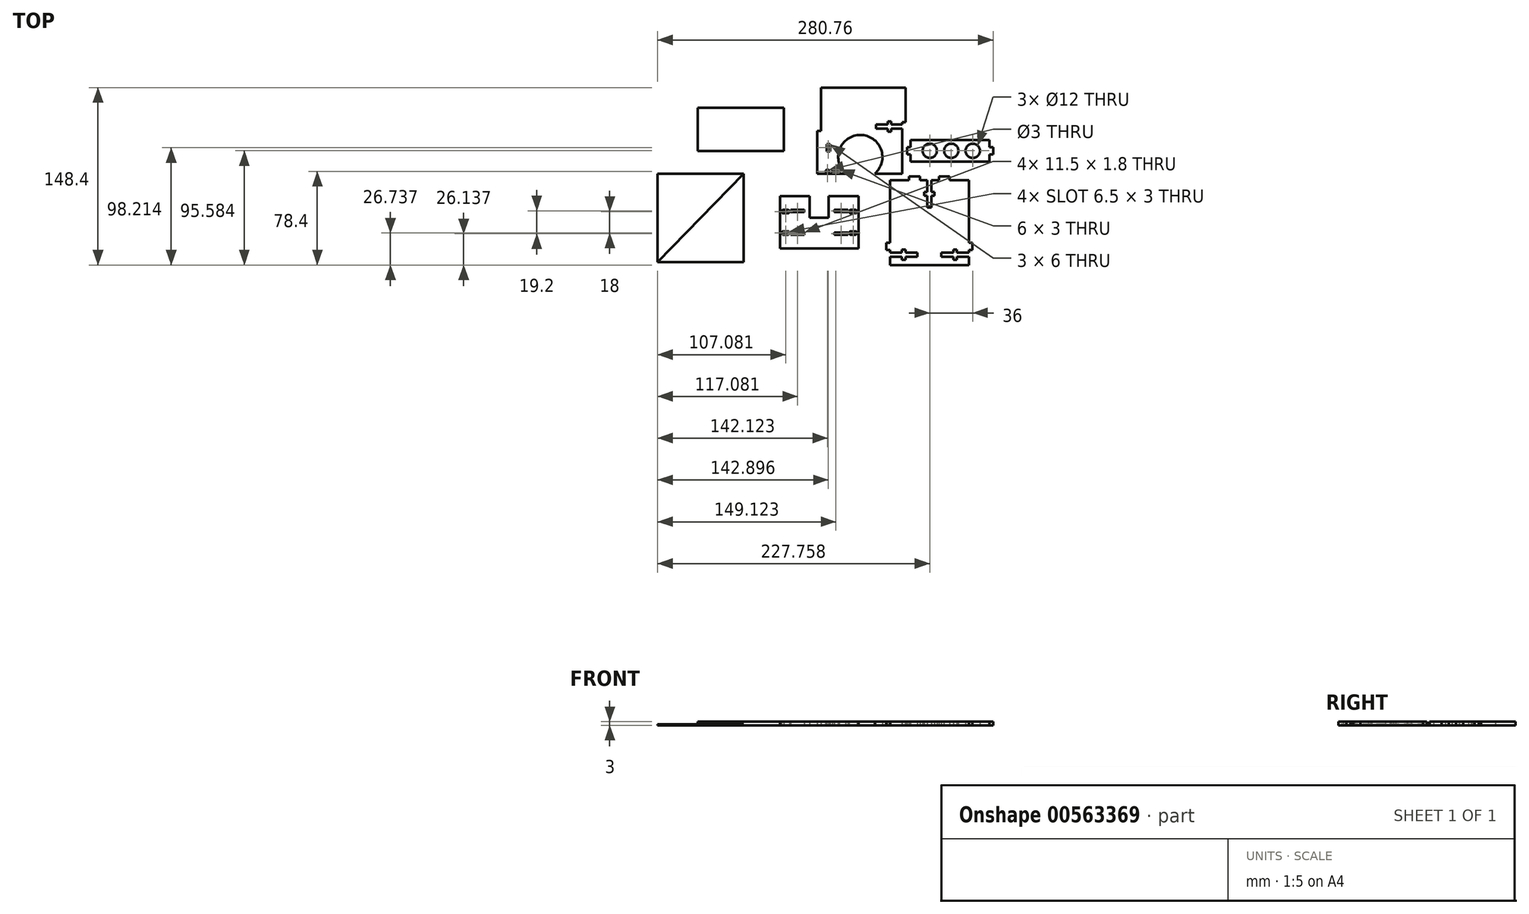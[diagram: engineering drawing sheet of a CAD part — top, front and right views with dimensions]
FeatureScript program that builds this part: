
annotation { "Feature Type Name" : "Feature", "Feature Type Description" : "" }
export const myFeature = defineFeature(function(context is Context, id is Id, definition is map)
    precondition{}
    {
        {
            var Q0;
            Q0=qCreatedBy(makeId("Top.planeOp"),FACE);
            var sketch = newSketch(context, id + "F0", { "sketchPlane" : qUnion([Q0])});
            skLineSegment(sketch, "E0", {"start": v(0, 0) * mm, "end": v(31.91, 0) * mm});
            skLineSegment(sketch, "E1", {"start": v(31.91, 0) * mm, "end": v(31.91, 36) * mm});
            skLineSegment(sketch, "E2", {"start": v(31.91, 36) * mm, "end": v(34.91, 36) * mm});
            skLineSegment(sketch, "E3", {"start": v(34.91, 36) * mm, "end": v(34.91, 72) * mm});
            skLineSegment(sketch, "E4", {"start": v(34.91, 72) * mm, "end": v(-36.09, 72) * mm});
            skLineSegment(sketch, "E5", {"start": v(-36.09, 72) * mm, "end": v(-36.09, 36) * mm});
            skLineSegment(sketch, "E6", {"start": v(-36.09, 36) * mm, "end": v(-39.09, 36) * mm});
            skLineSegment(sketch, "E7", {"start": v(-39.09, 36) * mm, "end": v(-39.09, 0) * mm});
            skLineSegment(sketch, "E8", {"start": v(-39.09, 0) * mm, "end": v(0, 0) * mm});
            skSolve(sketch);
        }
        {
            var Q0;
            Q0=makeQuery(id+"F0.imprint","IMPRINT",FACE,{"disambiguationData":[TD([[makeQuery(id+"F0.imprint","IMPRINT",EDGE,{"derivedFrom":sQuery(id+"F0.wireOp",EDGE,"E0")}),1.0]])]});
            extrude(context, id + "F1", {"entities" : qUnion([Q0]), "depth" : 3 * mm});
        }
        {
            var Q0;
            Q0=makeQuery(id+"F0.imprint","IMPRINT",FACE,{"disambiguationData":[TD([[makeQuery(id+"F0.imprint","IMPRINT",EDGE,{"derivedFrom":sQuery(id+"F0.wireOp",EDGE,"E0")}),1.0]])]});
            var sketch = newSketch(context, id + "F2", { "sketchPlane" : qUnion([Q0])});
            skCircle(sketch, "E9", {"center": v(-3.09, 14) * mm, "radius": 18.5 * mm});
            skCircle(sketch, "E10", {"center": v(-30.59, 2) * mm, "radius": 1.5 * mm});
            skLineSegment(sketch, "E11.bottom", {"start": v(-26.59, 3.5) * mm, "end": v(-20.59, 3.5) * mm});
            skLineSegment(sketch, "E11.top", {"start": v(-26.59, 0.5) * mm, "end": v(-20.59, 0.5) * mm});
            skLineSegment(sketch, "E11.left", {"start": v(-26.59, 3.5) * mm, "end": v(-26.59, 0.5) * mm});
            skLineSegment(sketch, "E11.right", {"start": v(-20.59, 3.5) * mm, "end": v(-20.59, 0.5) * mm});
            skLineSegment(sketch, "E12.bottom", {"start": v(-31.31, 24.81) * mm, "end": v(-28.31, 24.81) * mm});
            skLineSegment(sketch, "E12.top", {"start": v(-31.31, 18.81) * mm, "end": v(-28.31, 18.81) * mm});
            skLineSegment(sketch, "E12.left", {"start": v(-31.31, 24.81) * mm, "end": v(-31.31, 18.81) * mm});
            skLineSegment(sketch, "E12.right", {"start": v(-28.31, 24.81) * mm, "end": v(-28.31, 18.81) * mm});
            skSolve(sketch);
        }
        {
            var Q0;
            Q0=qSketchRegion(id+"F2",true);
            extrude(context, id + "F3", {"entities" : qUnion([Q0]), "operationType" : NewBodyOperationType.REMOVE, "endBound" : BoundingType.UP_TO_NEXT, "depth" : 25 * mm});
        }
        {
            var Q0;
            Q0=makeQuery(id+"F1.opExtrude","CAP_FACE",FACE,{"disambiguationData":[OSD([sQuery(id+"F0.wireOp",EDGE,"E0"),sQuery(id+"F0.wireOp",EDGE,"E1"),sQuery(id+"F0.wireOp",EDGE,"E2"),sQuery(id+"F0.wireOp",EDGE,"E3"),sQuery(id+"F0.wireOp",EDGE,"E4"),sQuery(id+"F0.wireOp",EDGE,"E5"),sQuery(id+"F0.wireOp",EDGE,"E6"),sQuery(id+"F0.wireOp",EDGE,"E7"),sQuery(id+"F0.wireOp",EDGE,"E8")])],"isStart":false});
            var sketch = newSketch(context, id + "F4", { "sketchPlane" : qUnion([Q0])});
            skLineSegment(sketch, "E13", {"start": v(22.91, 41.25) * mm, "end": v(22.91, 43.75) * mm});
            skLineSegment(sketch, "E14", {"start": v(22.91, 43.75) * mm, "end": v(19.91, 43.75) * mm});
            skLineSegment(sketch, "E15", {"start": v(19.91, 43.75) * mm, "end": v(19.91, 41.25) * mm});
            skLineSegment(sketch, "E16", {"start": v(19.91, 41.25) * mm, "end": v(9.91, 41.25) * mm});
            skLineSegment(sketch, "E17", {"start": v(9.91, 41.25) * mm, "end": v(9.91, 37.75) * mm});
            skLineSegment(sketch, "E18", {"start": v(9.91, 37.75) * mm, "end": v(19.91, 37.75) * mm});
            skLineSegment(sketch, "E19", {"start": v(19.91, 37.75) * mm, "end": v(19.91, 35.25) * mm});
            skLineSegment(sketch, "E20", {"start": v(19.91, 35.25) * mm, "end": v(22.91, 35.25) * mm});
            skLineSegment(sketch, "E21", {"start": v(22.91, 35.25) * mm, "end": v(22.91, 37.75) * mm});
            skLineSegment(sketch, "E22", {"start": v(22.91, 41.25) * mm, "end": v(31.91, 41.25) * mm});
            skLineSegment(sketch, "E23", {"start": v(31.91, 36) * mm, "end": v(31.91, 37.75) * mm});
            skLineSegment(sketch, "E24", {"start": v(31.91, 37.75) * mm, "end": v(22.91, 37.75) * mm});
            skLineSegment(sketch, "E25", {"start": v(31.91, 41.25) * mm, "end": v(31.91, 43) * mm});
            skLineSegment(sketch, "E26", {"start": v(31.91, 43) * mm, "end": v(34.91, 43) * mm});
            skLineSegment(sketch, "E27", {"start": v(31.91, 36) * mm, "end": v(34.91, 36) * mm});
            skLineSegment(sketch, "E28", {"start": v(34.91, 36) * mm, "end": v(34.91, 43) * mm});
            skSolve(sketch);
        }
        {
            var Q0;
            Q0=makeQuery(id+"F4.imprint","IMPRINT",FACE,{"disambiguationData":[TD([[makeQuery(id+"F4.imprint","IMPRINT",EDGE,{"derivedFrom":sQuery(id+"F4.wireOp",EDGE,"E13")}),1.0]])]});
            var Q1;
            Q1=makeQuery(id+"F4.imprint","IMPRINT",FACE,{"disambiguationData":[TD([[makeQuery(id+"F4.imprint","IMPRINT",EDGE,{"derivedFrom":sQuery(id+"F4.wireOp",EDGE,"a1bc5330-3307-4b1e-8fa0-ecfa6d1ff466.1.0.0")}),1.0]])]});
            extrude(context, id + "F5", {"entities" : qUnion([Q0, Q1]), "operationType" : NewBodyOperationType.REMOVE, "endBound" : BoundingType.UP_TO_NEXT, "oppositeDirection" : true, "depth" : 25 * mm});
        }
        {
            var Q0;
            Q0=qCreatedBy(makeId("Top.planeOp"),FACE);
            var sketch = newSketch(context, id + "F6", { "sketchPlane" : qUnion([Q0])});
            skLineSegment(sketch, "E29.bottom", {"start": v(-70.38, -18.66) * mm, "end": v(-4.38, -18.66) * mm});
            skLineSegment(sketch, "E29.top", {"start": v(-70.38, -62.66) * mm, "end": v(-4.38, -62.66) * mm});
            skLineSegment(sketch, "E29.left", {"start": v(-70.38, -18.66) * mm, "end": v(-70.38, -62.66) * mm});
            skLineSegment(sketch, "E29.right", {"start": v(-4.38, -18.66) * mm, "end": v(-4.38, -62.66) * mm});
            skLineSegment(sketch, "E30.bottom", {"start": v(-61.38, -30.16) * mm, "end": v(-49.88, -30.16) * mm});
            skLineSegment(sketch, "E30.top", {"start": v(-61.38, -31.96) * mm, "end": v(-49.88, -31.96) * mm});
            skLineSegment(sketch, "E30.left", {"start": v(-61.38, -30.16) * mm, "end": v(-61.38, -31.96) * mm});
            skLineSegment(sketch, "E30.right", {"start": v(-49.88, -30.16) * mm, "end": v(-49.88, -31.96) * mm});
            skLineSegment(sketch, "E31.bottom", {"start": v(-67.38, -30.16) * mm, "end": v(-63.88, -30.16) * mm});
            skLineSegment(sketch, "E31.top", {"start": v(-67.38, -33.16) * mm, "end": v(-63.88, -33.16) * mm});
            skLineSegment(sketch, "E31.left", {"start": v(-68.88, -31.66) * mm, "end": v(-68.88, -31.66) * mm});
            skLineSegment(sketch, "E31.right", {"start": v(-62.38, -31.66) * mm, "end": v(-62.38, -31.66) * mm});
            skPoint(sketch, "E32.visualSharp", {"position": v(-68.88, -30.16) * mm});
            skArc(sketch, "E32.filletArc", {"start": v(-67.38, -30.16) * mm, "mid": v(-68.44, -30.6) * mm, "end": v(-68.88, -31.66) * mm});
            skPoint(sketch, "E33.visualSharp", {"position": v(-68.88, -33.16) * mm});
            skArc(sketch, "E33.filletArc", {"start": v(-68.88, -31.66) * mm, "mid": v(-68.44, -32.72) * mm, "end": v(-67.38, -33.16) * mm});
            skPoint(sketch, "E34.visualSharp", {"position": v(-62.38, -33.16) * mm});
            skArc(sketch, "E34.filletArc", {"start": v(-63.88, -33.16) * mm, "mid": v(-62.82, -32.72) * mm, "end": v(-62.38, -31.66) * mm});
            skPoint(sketch, "E35.visualSharp", {"position": v(-62.38, -30.16) * mm});
            skArc(sketch, "E35.filletArc", {"start": v(-62.38, -31.66) * mm, "mid": v(-62.82, -30.6) * mm, "end": v(-63.88, -30.16) * mm});
            skLineSegment(sketch, "E36", {"start": v(-70.38, -40.66) * mm, "end": v(-4.38, -40.66) * mm, "construction": true});
            skLineSegment(sketch, "E37", {"start": v(-37.38, -18.66) * mm, "end": v(-37.38, -62.66) * mm, "construction": true});
            skArc(sketch, "E38.MirrorCS", {"start": v(-12.38, -31.66) * mm, "mid": v(-11.94, -30.6) * mm, "end": v(-10.88, -30.16) * mm});
            skLineSegment(sketch, "E39.MirrorCS", {"start": v(-24.88, -30.16) * mm, "end": v(-24.88, -31.96) * mm});
            skLineSegment(sketch, "E40.MirrorCS", {"start": v(-13.38, -30.16) * mm, "end": v(-13.38, -31.96) * mm});
            skArc(sketch, "E41.MirrorCS", {"start": v(-10.88, -33.16) * mm, "mid": v(-11.94, -32.72) * mm, "end": v(-12.38, -31.66) * mm});
            skArc(sketch, "E42.MirrorCS", {"start": v(-5.88, -31.66) * mm, "mid": v(-6.32, -32.72) * mm, "end": v(-7.38, -33.16) * mm});
            skArc(sketch, "E43.MirrorCS", {"start": v(-7.38, -30.16) * mm, "mid": v(-6.32, -30.6) * mm, "end": v(-5.88, -31.66) * mm});
            skLineSegment(sketch, "E44.MirrorCS", {"start": v(-7.38, -30.16) * mm, "end": v(-10.88, -30.16) * mm});
            skLineSegment(sketch, "E45.MirrorCS", {"start": v(-7.38, -33.16) * mm, "end": v(-10.88, -33.16) * mm});
            skLineSegment(sketch, "E46.MirrorCS", {"start": v(-13.38, -30.16) * mm, "end": v(-24.88, -30.16) * mm});
            skLineSegment(sketch, "E47.MirrorCS", {"start": v(-13.38, -31.96) * mm, "end": v(-24.88, -31.96) * mm});
            skPoint(sketch, "E48.MirrorP", {"position": v(-12.38, -33.16) * mm});
            skPoint(sketch, "E49.MirrorP", {"position": v(-12.38, -30.16) * mm});
            skPoint(sketch, "E50.MirrorP", {"position": v(-5.88, -30.16) * mm});
            skPoint(sketch, "E51.MirrorP", {"position": v(-5.88, -33.16) * mm});
            skLineSegment(sketch, "E52.MirrorCS", {"start": v(-7.38, -51.16) * mm, "end": v(-10.88, -51.16) * mm});
            skLineSegment(sketch, "E53.MirrorCS", {"start": v(-7.38, -48.16) * mm, "end": v(-10.88, -48.16) * mm});
            skLineSegment(sketch, "E54.MirrorCS", {"start": v(-13.38, -51.16) * mm, "end": v(-24.88, -51.16) * mm});
            skLineSegment(sketch, "E55.MirrorCS", {"start": v(-13.38, -49.36) * mm, "end": v(-24.88, -49.36) * mm});
            skArc(sketch, "E56.MirrorCS", {"start": v(-62.38, -49.66) * mm, "mid": v(-62.82, -50.72) * mm, "end": v(-63.88, -51.16) * mm});
            skArc(sketch, "E57.MirrorCS", {"start": v(-63.88, -48.16) * mm, "mid": v(-62.82, -48.6) * mm, "end": v(-62.38, -49.66) * mm});
            skArc(sketch, "E58.MirrorCS", {"start": v(-68.88, -49.66) * mm, "mid": v(-68.44, -48.6) * mm, "end": v(-67.38, -48.16) * mm});
            skLineSegment(sketch, "E59.MirrorCS", {"start": v(-61.38, -51.16) * mm, "end": v(-61.38, -49.36) * mm});
            skLineSegment(sketch, "E60.MirrorCS", {"start": v(-49.88, -51.16) * mm, "end": v(-49.88, -49.36) * mm});
            skArc(sketch, "E61.MirrorCS", {"start": v(-67.38, -51.16) * mm, "mid": v(-68.44, -50.72) * mm, "end": v(-68.88, -49.66) * mm});
            skPoint(sketch, "E62.MirrorP", {"position": v(-62.38, -48.16) * mm});
            skPoint(sketch, "E63.MirrorP", {"position": v(-68.88, -48.16) * mm});
            skPoint(sketch, "E64.MirrorP", {"position": v(-62.38, -51.16) * mm});
            skLineSegment(sketch, "E65.MirrorCS", {"start": v(-67.38, -51.16) * mm, "end": v(-63.88, -51.16) * mm});
            skPoint(sketch, "E66.MirrorP", {"position": v(-68.88, -51.16) * mm});
            skLineSegment(sketch, "E67.MirrorCS", {"start": v(-67.38, -48.16) * mm, "end": v(-63.88, -48.16) * mm});
            skLineSegment(sketch, "E68.MirrorCS", {"start": v(-61.38, -49.36) * mm, "end": v(-49.88, -49.36) * mm});
            skLineSegment(sketch, "E69.MirrorCS", {"start": v(-61.38, -51.16) * mm, "end": v(-49.88, -51.16) * mm});
            skArc(sketch, "E70.MirrorCS", {"start": v(-7.38, -51.16) * mm, "mid": v(-6.32, -50.72) * mm, "end": v(-5.88, -49.66) * mm});
            skLineSegment(sketch, "E71.MirrorCS", {"start": v(-13.38, -51.16) * mm, "end": v(-13.38, -49.36) * mm});
            skLineSegment(sketch, "E72.MirrorCS", {"start": v(-24.88, -51.16) * mm, "end": v(-24.88, -49.36) * mm});
            skArc(sketch, "E73.MirrorCS", {"start": v(-10.88, -48.16) * mm, "mid": v(-11.94, -48.6) * mm, "end": v(-12.38, -49.66) * mm});
            skArc(sketch, "E74.MirrorCS", {"start": v(-12.38, -49.66) * mm, "mid": v(-11.94, -50.72) * mm, "end": v(-10.88, -51.16) * mm});
            skArc(sketch, "E75.MirrorCS", {"start": v(-5.88, -49.66) * mm, "mid": v(-6.32, -48.6) * mm, "end": v(-7.38, -48.16) * mm});
            skLineSegment(sketch, "E76.bottom", {"start": v(-45.43, -18.66) * mm, "end": v(-29.7, -18.66) * mm});
            skLineSegment(sketch, "E76.top", {"start": v(-45.43, -36.8) * mm, "end": v(-29.7, -36.8) * mm});
            skLineSegment(sketch, "E76.left", {"start": v(-45.43, -18.66) * mm, "end": v(-45.43, -36.8) * mm});
            skLineSegment(sketch, "E76.right", {"start": v(-29.7, -18.66) * mm, "end": v(-29.7, -36.8) * mm});
            skSolve(sketch);
        }
        {
            var Q0;
            Q0=makeQuery(id+"F6.imprint","IMPRINT",FACE,{"disambiguationData":[TD([[makeQuery(id+"F6.imprint","IMPRINT",EDGE,{"derivedFrom":sQuery(id+"F6.wireOp",EDGE,"E29.bottom")}),-1.0]])]});
            extrude(context, id + "F7", {"entities" : qUnion([Q0]), "depth" : 3 * mm});
        }
        {
            var Q0;
            Q0=qCreatedBy(makeId("Top.planeOp"),FACE);
            var sketch = newSketch(context, id + "F8", { "sketchPlane" : qUnion([Q0])});
            skLineSegment(sketch, "E77.bottom", {"start": v(-67.1, 19.07) * mm, "end": v(-139.1, 19.07) * mm});
            skLineSegment(sketch, "E77.top", {"start": v(-67.1, 55.07) * mm, "end": v(-139.1, 55.07) * mm});
            skLineSegment(sketch, "E77.left", {"start": v(-67.1, 19.07) * mm, "end": v(-67.1, 55.07) * mm});
            skLineSegment(sketch, "E77.right", {"start": v(-139.1, 19.07) * mm, "end": v(-139.1, 55.07) * mm});
            skSolve(sketch);
        }
        {
            var Q0;
            Q0=makeQuery(id+"F8.imprint","IMPRINT",FACE,{"disambiguationData":[TD([[makeQuery(id+"F8.imprint","IMPRINT",EDGE,{"derivedFrom":sQuery(id+"F8.wireOp",EDGE,"E77.bottom")}),-1.0]])]});
            extrude(context, id + "F9", {"entities" : qUnion([Q0]), "depth" : 3 * mm});
        }
        {
            var Q0;
            Q0=qCreatedBy(makeId("Top.planeOp"),FACE);
            var sketch = newSketch(context, id + "F10", { "sketchPlane" : qUnion([Q0])});
            skLineSegment(sketch, "E78.bottom", {"start": v(21.76, -5.4) * mm, "end": v(37.76, -5.4) * mm});
            skLineSegment(sketch, "E78.top", {"start": v(21.76, -76.4) * mm, "end": v(87.76, -76.4) * mm});
            skLineSegment(sketch, "E78.left", {"start": v(21.76, -5.4) * mm, "end": v(21.76, -57.9) * mm});
            skLineSegment(sketch, "E78.right", {"start": v(87.76, -5.4) * mm, "end": v(87.76, -57.9) * mm});
            skLineSegment(sketch, "E79", {"start": v(53.01, -5.4) * mm, "end": v(53.01, -15.4) * mm});
            skLineSegment(sketch, "E80", {"start": v(53.01, -15.4) * mm, "end": v(50.51, -15.4) * mm});
            skLineSegment(sketch, "E81", {"start": v(50.51, -15.4) * mm, "end": v(50.51, -18.4) * mm});
            skLineSegment(sketch, "E82", {"start": v(50.51, -18.4) * mm, "end": v(53.01, -18.4) * mm});
            skLineSegment(sketch, "E83", {"start": v(53.01, -18.4) * mm, "end": v(53.01, -28.4) * mm});
            skLineSegment(sketch, "E84", {"start": v(53.01, -28.4) * mm, "end": v(56.51, -28.4) * mm});
            skLineSegment(sketch, "E85", {"start": v(56.51, -28.4) * mm, "end": v(56.51, -18.4) * mm});
            skLineSegment(sketch, "E86", {"start": v(56.51, -18.4) * mm, "end": v(59.01, -18.4) * mm});
            skLineSegment(sketch, "E87", {"start": v(59.01, -18.4) * mm, "end": v(59.01, -15.4) * mm});
            skLineSegment(sketch, "E88", {"start": v(59.01, -15.4) * mm, "end": v(56.51, -15.4) * mm});
            skLineSegment(sketch, "E89", {"start": v(56.51, -15.4) * mm, "end": v(56.51, -5.4) * mm});
            skLineSegment(sketch, "E90", {"start": v(50.51, -15.4) * mm, "end": v(21.76, -15.4) * mm, "construction": true});
            skLineSegment(sketch, "E91", {"start": v(59.01, -15.4) * mm, "end": v(87.76, -15.4) * mm, "construction": true});
            skLineSegment(sketch, "E92", {"start": v(21.76, -69.65) * mm, "end": v(31.76, -69.65) * mm});
            skLineSegment(sketch, "E93", {"start": v(31.76, -69.65) * mm, "end": v(31.76, -72.15) * mm});
            skLineSegment(sketch, "E94", {"start": v(31.76, -72.15) * mm, "end": v(34.76, -72.15) * mm});
            skLineSegment(sketch, "E95", {"start": v(34.76, -72.15) * mm, "end": v(34.76, -69.65) * mm});
            skLineSegment(sketch, "E96", {"start": v(34.76, -69.65) * mm, "end": v(44.76, -69.65) * mm});
            skLineSegment(sketch, "E97", {"start": v(44.76, -69.65) * mm, "end": v(44.76, -66.15) * mm});
            skLineSegment(sketch, "E98", {"start": v(44.76, -66.15) * mm, "end": v(34.76, -66.15) * mm});
            skLineSegment(sketch, "E99", {"start": v(34.76, -66.15) * mm, "end": v(34.76, -63.65) * mm});
            skLineSegment(sketch, "E100", {"start": v(34.76, -63.65) * mm, "end": v(31.76, -63.65) * mm});
            skLineSegment(sketch, "E101", {"start": v(31.76, -63.65) * mm, "end": v(31.76, -66.15) * mm});
            skLineSegment(sketch, "E102", {"start": v(31.76, -66.15) * mm, "end": v(21.76, -66.15) * mm});
            skLineSegment(sketch, "E103", {"start": v(54.76, -76.4) * mm, "end": v(54.76, -55.52) * mm, "construction": true});
            skLineSegment(sketch, "E104.MirrorCS", {"start": v(74.76, -63.65) * mm, "end": v(77.76, -63.65) * mm});
            skLineSegment(sketch, "E105.MirrorCS", {"start": v(77.76, -69.65) * mm, "end": v(77.76, -72.15) * mm});
            skLineSegment(sketch, "E106.MirrorCS", {"start": v(77.76, -66.15) * mm, "end": v(87.76, -66.15) * mm});
            skLineSegment(sketch, "E107.MirrorCS", {"start": v(74.76, -72.15) * mm, "end": v(74.76, -69.65) * mm});
            skLineSegment(sketch, "E108.MirrorCS", {"start": v(77.76, -72.15) * mm, "end": v(74.76, -72.15) * mm});
            skLineSegment(sketch, "E109.MirrorCS", {"start": v(74.76, -69.65) * mm, "end": v(64.76, -69.65) * mm});
            skLineSegment(sketch, "E110.MirrorCS", {"start": v(64.76, -66.15) * mm, "end": v(74.76, -66.15) * mm});
            skLineSegment(sketch, "E111.MirrorCS", {"start": v(74.76, -66.15) * mm, "end": v(74.76, -63.65) * mm});
            skLineSegment(sketch, "E112.MirrorCS", {"start": v(87.76, -69.65) * mm, "end": v(77.76, -69.65) * mm});
            skLineSegment(sketch, "E113.MirrorCS", {"start": v(64.76, -69.65) * mm, "end": v(64.76, -66.15) * mm});
            skLineSegment(sketch, "E114.MirrorCS", {"start": v(77.76, -63.65) * mm, "end": v(77.76, -66.15) * mm});
            skLineSegment(sketch, "E115.bottom", {"start": v(87.76, -63.9) * mm, "end": v(90.76, -63.9) * mm});
            skLineSegment(sketch, "E115.top", {"start": v(87.76, -57.9) * mm, "end": v(90.76, -57.9) * mm});
            skLineSegment(sketch, "E115.right", {"start": v(90.76, -63.9) * mm, "end": v(90.76, -57.9) * mm});
            skLineSegment(sketch, "E116.trimOffspring", {"start": v(87.76, -63.9) * mm, "end": v(87.76, -76.4) * mm});
            skLineSegment(sketch, "E117.MirrorCS", {"start": v(21.76, -63.9) * mm, "end": v(18.76, -63.9) * mm});
            skLineSegment(sketch, "E118.MirrorCS", {"start": v(21.76, -57.9) * mm, "end": v(18.76, -57.9) * mm});
            skLineSegment(sketch, "E119.MirrorCS", {"start": v(18.76, -63.9) * mm, "end": v(18.76, -57.9) * mm});
            skLineSegment(sketch, "E120.trimOffspring", {"start": v(21.76, -63.9) * mm, "end": v(21.76, -76.4) * mm});
            skLineSegment(sketch, "E121.top", {"start": v(62.76, -2.4) * mm, "end": v(71.76, -2.4) * mm});
            skLineSegment(sketch, "E121.left", {"start": v(62.76, -5.4) * mm, "end": v(62.76, -2.4) * mm});
            skLineSegment(sketch, "E121.right", {"start": v(71.76, -5.4) * mm, "end": v(71.76, -2.4) * mm});
            skLineSegment(sketch, "E122", {"start": v(54.76, -5.4) * mm, "end": v(54.76, -1.03) * mm, "construction": true});
            skLineSegment(sketch, "E123.trimOffspring", {"start": v(71.76, -5.4) * mm, "end": v(87.76, -5.4) * mm});
            skLineSegment(sketch, "E124.MirrorCS", {"start": v(46.76, -5.4) * mm, "end": v(46.76, -2.4) * mm});
            skLineSegment(sketch, "E125.MirrorCS", {"start": v(37.76, -5.4) * mm, "end": v(37.76, -2.4) * mm});
            skLineSegment(sketch, "E126.MirrorCS", {"start": v(46.76, -2.4) * mm, "end": v(37.76, -2.4) * mm});
            skLineSegment(sketch, "E127.trimOffspring", {"start": v(46.76, -5.4) * mm, "end": v(62.76, -5.4) * mm});
            skSolve(sketch);
        }
        {
            var Q0;
            Q0=makeQuery(id+"F10.imprint","IMPRINT",FACE,{"disambiguationData":[TD([[makeQuery(id+"F10.imprint","IMPRINT",EDGE,{"derivedFrom":sQuery(id+"F10.wireOp",EDGE,"E78.bottom")}),-1.0]])]});
            extrude(context, id + "F11", {"entities" : qUnion([Q0]), "depth" : 3 * mm});
        }
        {
            var Q0;
            Q0=qCreatedBy(makeId("Top.planeOp"),FACE);
            var sketch = newSketch(context, id + "F12", { "sketchPlane" : qUnion([Q0])});
            skLineSegment(sketch, "E128.bottom", {"start": v(-172.7, -0.16) * mm, "end": v(-100.7, -0.16) * mm});
            skLineSegment(sketch, "E128.top", {"start": v(-172.7, -74.16) * mm, "end": v(-100.7, -74.16) * mm});
            skLineSegment(sketch, "E128.left", {"start": v(-172.7, -0.16) * mm, "end": v(-172.7, -74.16) * mm});
            skLineSegment(sketch, "E128.right", {"start": v(-100.7, -0.16) * mm, "end": v(-100.7, -74.16) * mm});
            skLineSegment(sketch, "E129", {"start": v(-172.7, -74.16) * mm, "end": v(-100.7, -0.16) * mm});
            skSolve(sketch);
        }
        {
            var Q0;
            Q0=makeQuery(id+"F12.imprint","IMPRINT",FACE,{"disambiguationData":[TD([[makeQuery(id+"F12.imprint","IMPRINT",EDGE,{"derivedFrom":sQuery(id+"F12.wireOp",EDGE,"E128.bottom")}),-1.0]])]});
            extrude(context, id + "F13", {"entities" : qUnion([Q0]), "depth" : 1 * mm});
        }
        {
            var Q0;
            Q0=makeQuery(id+"F12.imprint","IMPRINT",FACE,{"disambiguationData":[TD([[makeQuery(id+"F12.imprint","IMPRINT",EDGE,{"derivedFrom":sQuery(id+"F12.wireOp",EDGE,"E128.top")}),1.0]])]});
            extrude(context, id + "F14", {"entities" : qUnion([Q0]), "depth" : 1 * mm});
        }
        {
            var Q0;
            Q0=qCreatedBy(makeId("Top.planeOp"),FACE);
            var sketch = newSketch(context, id + "F15", { "sketchPlane" : qUnion([Q0])});
            skLineSegment(sketch, "E130", {"start": v(36.05, 16.18) * mm, "end": v(36.05, 22.18) * mm});
            skLineSegment(sketch, "E131", {"start": v(36.05, 22.18) * mm, "end": v(39.05, 22.18) * mm});
            skLineSegment(sketch, "E132", {"start": v(39.05, 22.18) * mm, "end": v(39.05, 28.18) * mm});
            skLineSegment(sketch, "E133", {"start": v(39.05, 28.18) * mm, "end": v(105.05, 28.18) * mm});
            skLineSegment(sketch, "E134", {"start": v(105.05, 28.18) * mm, "end": v(105.05, 22.18) * mm});
            skLineSegment(sketch, "E135", {"start": v(105.05, 22.18) * mm, "end": v(108.05, 22.18) * mm});
            skLineSegment(sketch, "E136", {"start": v(108.05, 22.18) * mm, "end": v(108.05, 16.18) * mm});
            skLineSegment(sketch, "E137", {"start": v(108.05, 16.18) * mm, "end": v(105.05, 16.18) * mm});
            skLineSegment(sketch, "E138", {"start": v(105.05, 16.18) * mm, "end": v(105.05, 10.18) * mm});
            skLineSegment(sketch, "E139", {"start": v(105.05, 10.18) * mm, "end": v(39.05, 10.18) * mm});
            skLineSegment(sketch, "E140", {"start": v(39.05, 10.18) * mm, "end": v(39.05, 16.18) * mm});
            skLineSegment(sketch, "E141", {"start": v(39.05, 16.18) * mm, "end": v(36.05, 16.18) * mm});
            skCircle(sketch, "E142", {"center": v(55.05, 19.18) * mm, "radius": 6 * mm});
            skCircle(sketch, "E143.1.0.0", {"center": v(73.05, 19.18) * mm, "radius": 6 * mm});
            skCircle(sketch, "E143.2.0.0", {"center": v(91.05, 19.18) * mm, "radius": 6 * mm});
            skLineSegment(sketch, "E143.direction1", {"start": v(55.05, 19.18) * mm, "end": v(73.05, 19.18) * mm, "construction": true});
            skSolve(sketch);
        }
        {
            var Q0;
            Q0=makeQuery(id+"F15.imprint","IMPRINT",FACE,{"disambiguationData":[TD([[makeQuery(id+"F15.imprint","IMPRINT",EDGE,{"derivedFrom":sQuery(id+"F15.wireOp",EDGE,"E130")}),-1.0]])]});
            extrude(context, id + "F16", {"entities" : qUnion([Q0]), "depth" : 3 * mm});
        }
    });
